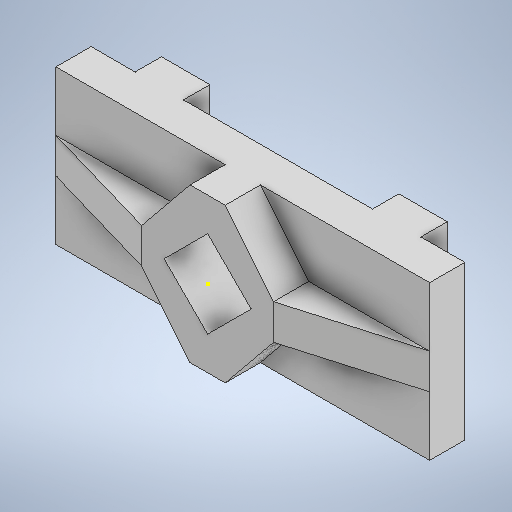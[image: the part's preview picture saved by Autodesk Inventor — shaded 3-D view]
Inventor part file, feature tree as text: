
AUTODESK INVENTOR PART (.ipt)
format: ipt  version: 2025.2 (Build 292293000, 293)  size: 344,576 bytes
history: native  units: in
note: dims shown in document units (in); Inventor stores cm internally (conversion verified against a paired STEP export)
features: sketch x7, extrude x4, rib x2, other x1
ambient origin geometry x8: Origin, YZ Plane, XZ Plane, XY Plane, X Axis, Y Axis, Z Axis, Center Point
bodies: Solid1 (feature_tree)
feature tree (14):
  extrude  "Extrusion1"  Depth=2.7559in
  extrude  "Extrusion2"  Depth=2.7559in
  extrude  "Extrusion3"  Depth=0.7874in
  rib  "Rib1"
  rib  "Rib2"
  extrude  "Extrusion4"  Depth=0.4724in
  sketch  "Sketch7"  dims[d25=1.063in d26=0.8661in d27=1.063in d28=0.8661in d29=1.063in d30=0.8661in d31=1.063in d32=0.6299in d33=0.0in d34=0.0394in d35=0.6299in d36=0.0in d37=0.0in d38=0.0394in d39=0.0394in d40=0.0394in d41=0.6299in d42=0.0in d43=0.0in d44=0.0394in d45=0.0394in d46=1.1024in d47=1.1024in d48=0.0in d49=0.0in]
  sketch  "Sketch1"  dims[d13=6.6929in d14=2.7559in]
  other  "Image1"
  sketch  "Sketch2"  dims[d15=0.6299in d16=0.0in d17=2.7559in]
  sketch  "Sketch3"  dims[d18=0.8661in d19=0.7874in]
  sketch  "Sketch4"  dims[d20=0.4724in d21=0.0in d22=2.3622in]
  sketch  "Sketch5"  dims[d23=2.7559in]
  sketch  "Sketch6"  dims[d24=0.8661in]
